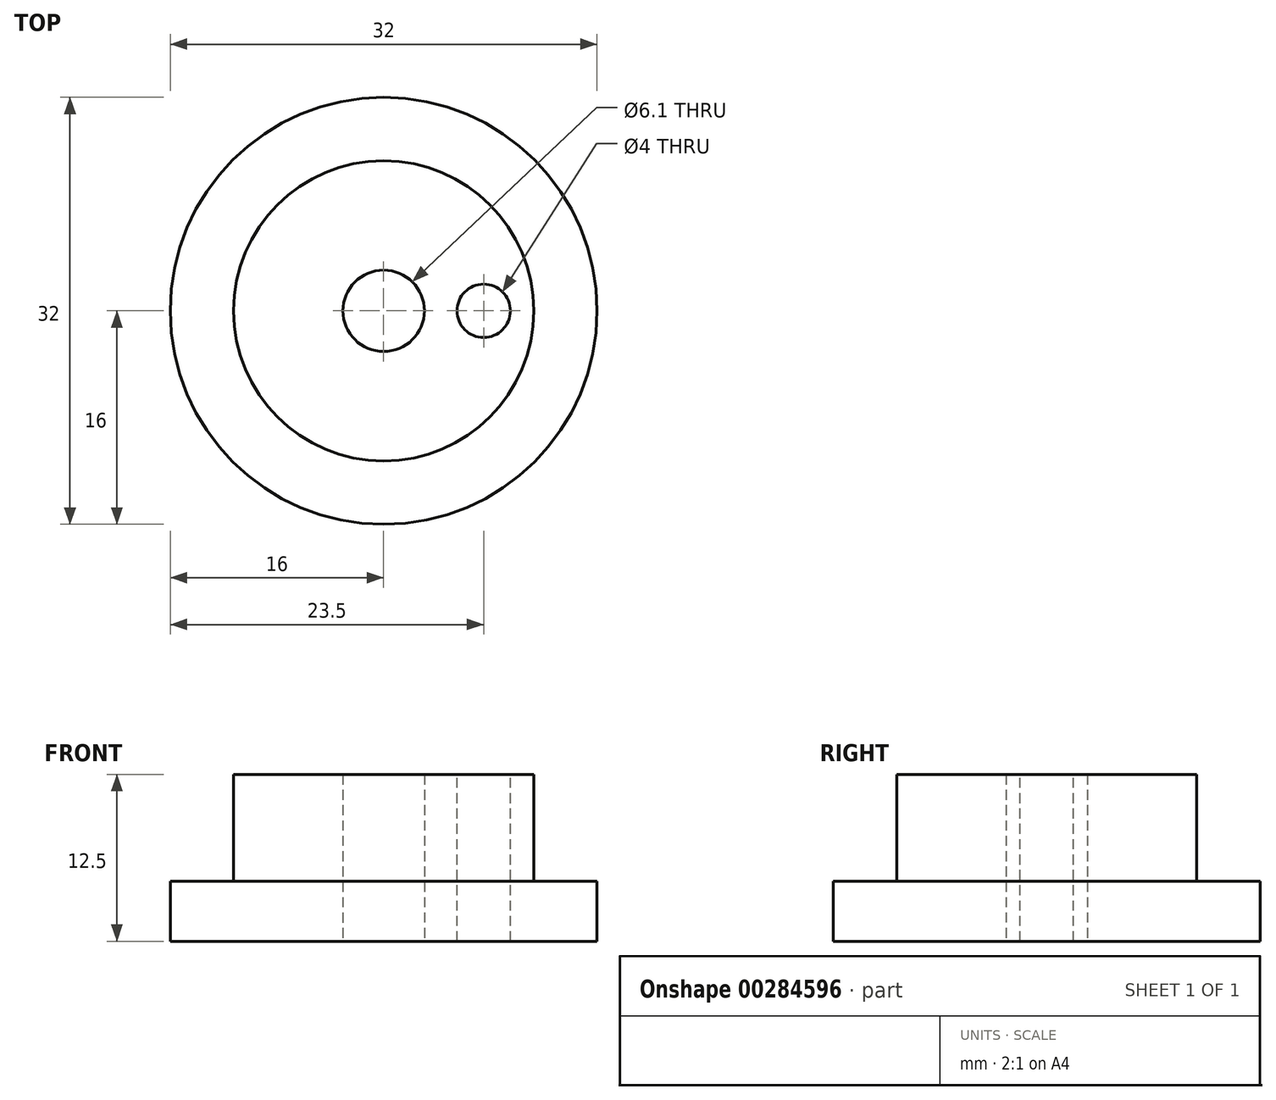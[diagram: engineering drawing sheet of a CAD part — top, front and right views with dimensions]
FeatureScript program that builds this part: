
annotation { "Feature Type Name" : "Feature", "Feature Type Description" : "" }
export const myFeature = defineFeature(function(context is Context, id is Id, definition is map)
    precondition{}
    {
        {
            var Q0;
            Q0=qCreatedBy(makeId("Front.planeOp"),FACE);
            var sketch = newSketch(context, id + "F0", { "sketchPlane" : qUnion([Q0])});
            skLineSegment(sketch, "E0", {"start": v(0, 0) * mm, "end": v(0, 45) * mm, "construction": true});
            skLineSegment(sketch, "E1", {"start": v(3.05, 12.5) * mm, "end": v(3.05, 0) * mm});
            skLineSegment(sketch, "E2", {"start": v(3.05, 0) * mm, "end": v(16, 0) * mm});
            skLineSegment(sketch, "E3", {"start": v(16, 0) * mm, "end": v(16, 4.5) * mm});
            skLineSegment(sketch, "E4", {"start": v(16, 4.5) * mm, "end": v(11.25, 4.5) * mm});
            skLineSegment(sketch, "E5", {"start": v(11.25, 4.5) * mm, "end": v(11.25, 12.5) * mm});
            skLineSegment(sketch, "E6", {"start": v(11.25, 12.5) * mm, "end": v(3.05, 12.5) * mm});
            skSolve(sketch);
        }
        {
            var Q0;
            Q0=qSketchRegion(id+"F0",true);
            var Q1;
            Q1=sQuery(id+"F0.wireOp",EDGE,"E0");
            revolve(context, id + "F1", {"entities" : qUnion([Q0]), "axis" : qUnion([Q1]), "revolveType" : RevolveType.FULL});
        }
        {
            var Q0;
            Q0=makeQuery(id+"F1.opRevolve","SWEPT_FACE",FACE,{"disambiguationData":[OSD([sQuery(id+"F0.wireOp",EDGE,"E6")])]});
            var sketch = newSketch(context, id + "F2", { "sketchPlane" : qUnion([Q0])});
            skPoint(sketch, "E7", {"position": v(7.5, 0) * mm});
            skSolve(sketch);
        }
        {
            var Q0;
            Q0=sQuery(id+"F2.wireOp",VERTEX,"E7");
            var Q1;
            Q1=makeQuery(id+"F1.opRevolve","SWEPT_BODY",BODY,{"disambiguationData":[OSD([sQuery(id+"F0.wireOp",EDGE,"E1"),sQuery(id+"F0.wireOp",EDGE,"E2"),sQuery(id+"F0.wireOp",EDGE,"E3"),sQuery(id+"F0.wireOp",EDGE,"E4"),sQuery(id+"F0.wireOp",EDGE,"E5"),sQuery(id+"F0.wireOp",EDGE,"E6")])]});
            hole(context, id + "F3", {"style" : HoleStyle.SIMPLE, "endStyle" : HoleEndStyle.THROUGH, "holeDiameter" : 4 * mm, "locations" : qUnion([Q0]), "scope" : qUnion([Q1]), "isTappedThrough" : true});
        }
    });
